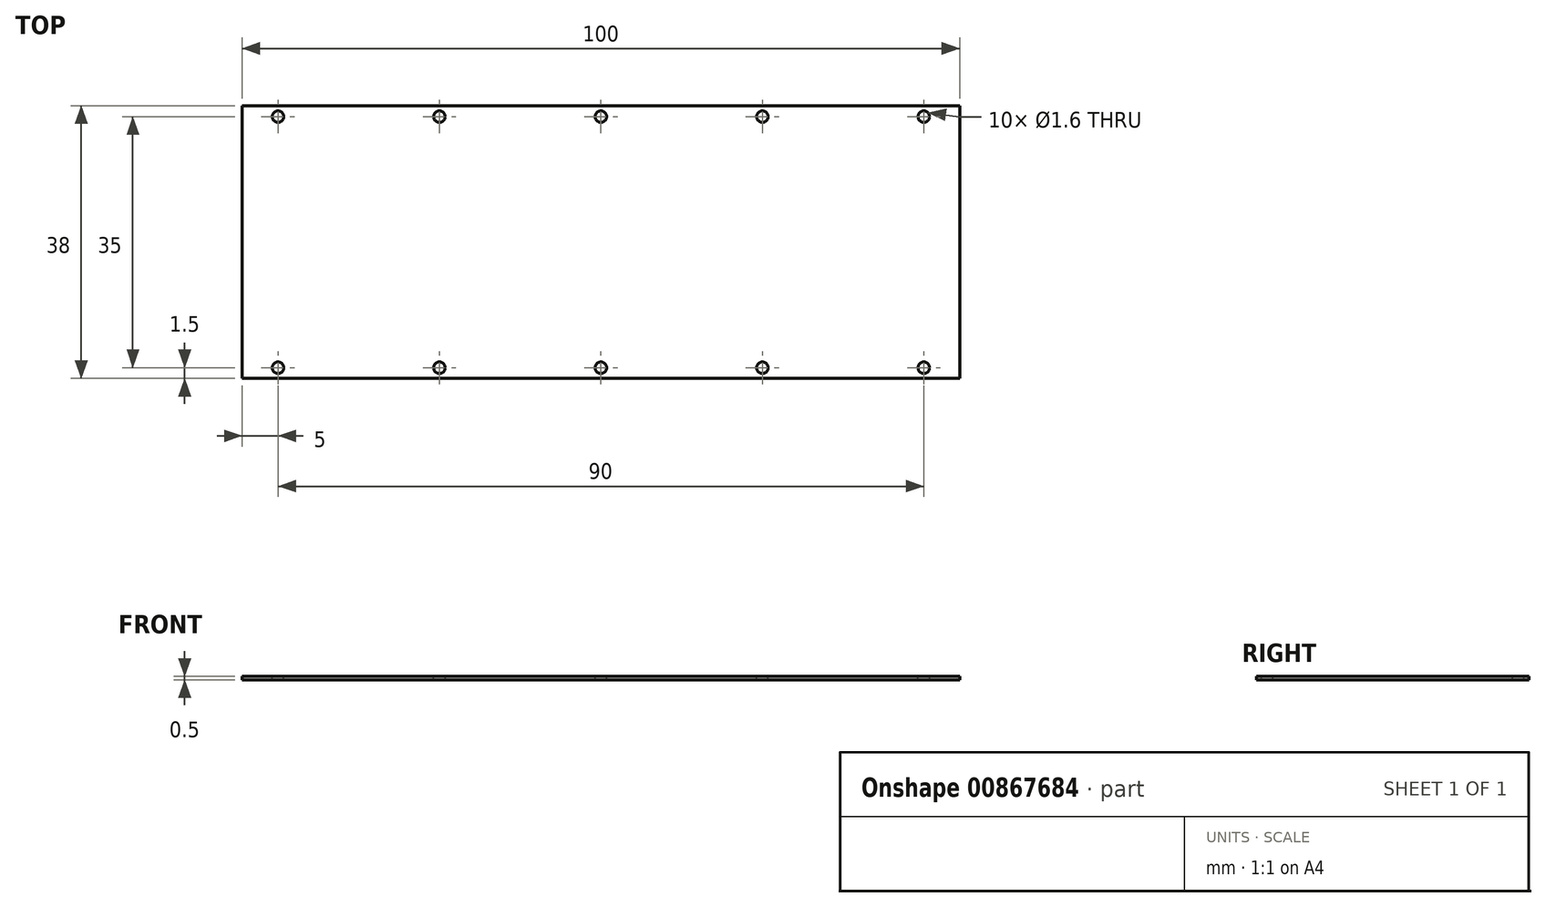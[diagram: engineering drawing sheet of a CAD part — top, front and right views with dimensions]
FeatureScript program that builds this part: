
annotation { "Feature Type Name" : "Feature", "Feature Type Description" : "" }
export const myFeature = defineFeature(function(context is Context, id is Id, definition is map)
    precondition{}
    {
        {
            var Q0;
            Q0=qCreatedBy(makeId("Top.planeOp"),FACE);
            var sketch = newSketch(context, id + "F0", { "sketchPlane" : qUnion([Q0])});
            skLineSegment(sketch, "E0.bottom", {"start": v(0, 19) * mm, "end": v(-100, 19) * mm});
            skLineSegment(sketch, "E0.top", {"start": v(0, -19) * mm, "end": v(-100, -19) * mm});
            skLineSegment(sketch, "E0.left", {"start": v(0, 19) * mm, "end": v(0, -19) * mm});
            skLineSegment(sketch, "E0.right", {"start": v(-100, 19) * mm, "end": v(-100, -19) * mm});
            skSolve(sketch);
        }
        {
            var Q0;
            Q0=makeQuery(id+"F0.imprint","IMPRINT",FACE,{"disambiguationData":[TD([[makeQuery(id+"F0.imprint","IMPRINT",EDGE,{"derivedFrom":sQuery(id+"F0.wireOp",EDGE,"E0.bottom")}),1.0]])]});
            extrude(context, id + "F1", {"entities" : qUnion([Q0]), "depth" : .5 * mm, "offsetDistance" : 25 * mm});
        }
        {
            var Q0;
            Q0=makeQuery(id+"F1.opExtrude","CAP_FACE",FACE,{"disambiguationData":[OSD([sQuery(id+"F0.wireOp",EDGE,"E0.bottom"),sQuery(id+"F0.wireOp",EDGE,"E0.top"),sQuery(id+"F0.wireOp",EDGE,"E0.left"),sQuery(id+"F0.wireOp",EDGE,"E0.right")])],"isStart":false});
            var sketch = newSketch(context, id + "F2", { "sketchPlane" : qUnion([Q0])});
            skCircle(sketch, "E1", {"center": v(-95, 17.5) * mm, "radius": 0.8 * mm});
            skCircle(sketch, "E2", {"center": v(-95, -17.5) * mm, "radius": 0.8 * mm});
            skCircle(sketch, "E3.1.0.0", {"center": v(-72.5, -17.5) * mm, "radius": 0.8 * mm});
            skCircle(sketch, "E3.2.0.0", {"center": v(-50, -17.5) * mm, "radius": 0.8 * mm});
            skCircle(sketch, "E3.3.0.0", {"center": v(-27.5, -17.5) * mm, "radius": 0.8 * mm});
            skCircle(sketch, "E3.4.0.0", {"center": v(-5, -17.5) * mm, "radius": 0.8 * mm});
            skLineSegment(sketch, "E3.direction1", {"start": v(-95, -17.5) * mm, "end": v(-72.5, -17.5) * mm, "construction": true});
            skCircle(sketch, "E4.1.0.0", {"center": v(-72.5, 17.5) * mm, "radius": 0.8 * mm});
            skCircle(sketch, "E4.2.0.0", {"center": v(-50, 17.5) * mm, "radius": 0.8 * mm});
            skCircle(sketch, "E4.3.0.0", {"center": v(-27.5, 17.5) * mm, "radius": 0.8 * mm});
            skCircle(sketch, "E4.4.0.0", {"center": v(-5, 17.5) * mm, "radius": 0.8 * mm});
            skLineSegment(sketch, "E4.direction1", {"start": v(-95, 17.5) * mm, "end": v(-72.5, 17.5) * mm, "construction": true});
            skSolve(sketch);
        }
        {
            var Q0;
            Q0=makeQuery(id+"F2.imprint","IMPRINT",FACE,{"disambiguationData":[TD([[makeQuery(id+"F2.imprint","IMPRINT",EDGE,{"derivedFrom":sQuery(id+"F2.wireOp",EDGE,"E2")}),1.0]])]});
            var Q1;
            Q1=makeQuery(id+"F2.imprint","IMPRINT",FACE,{"disambiguationData":[TD([[makeQuery(id+"F2.imprint","IMPRINT",EDGE,{"derivedFrom":sQuery(id+"F2.wireOp",EDGE,"E3.1.0.0")}),1.0]])]});
            var Q2;
            Q2=makeQuery(id+"F2.imprint","IMPRINT",FACE,{"disambiguationData":[TD([[makeQuery(id+"F2.imprint","IMPRINT",EDGE,{"derivedFrom":sQuery(id+"F2.wireOp",EDGE,"E3.2.0.0")}),1.0]])]});
            var Q3;
            Q3=makeQuery(id+"F2.imprint","IMPRINT",FACE,{"disambiguationData":[TD([[makeQuery(id+"F2.imprint","IMPRINT",EDGE,{"derivedFrom":sQuery(id+"F2.wireOp",EDGE,"E3.3.0.0")}),1.0]])]});
            var Q4;
            Q4=makeQuery(id+"F2.imprint","IMPRINT",FACE,{"disambiguationData":[TD([[makeQuery(id+"F2.imprint","IMPRINT",EDGE,{"derivedFrom":sQuery(id+"F2.wireOp",EDGE,"E3.4.0.0")}),1.0]])]});
            var Q5;
            Q5=makeQuery(id+"F2.imprint","IMPRINT",FACE,{"disambiguationData":[TD([[makeQuery(id+"F2.imprint","IMPRINT",EDGE,{"derivedFrom":sQuery(id+"F2.wireOp",EDGE,"E4.4.0.0")}),1.0]])]});
            var Q6;
            Q6=makeQuery(id+"F2.imprint","IMPRINT",FACE,{"disambiguationData":[TD([[makeQuery(id+"F2.imprint","IMPRINT",EDGE,{"derivedFrom":sQuery(id+"F2.wireOp",EDGE,"E4.3.0.0")}),1.0]])]});
            var Q7;
            Q7=makeQuery(id+"F2.imprint","IMPRINT",FACE,{"disambiguationData":[TD([[makeQuery(id+"F2.imprint","IMPRINT",EDGE,{"derivedFrom":sQuery(id+"F2.wireOp",EDGE,"E4.2.0.0")}),1.0]])]});
            var Q8;
            Q8=makeQuery(id+"F2.imprint","IMPRINT",FACE,{"disambiguationData":[TD([[makeQuery(id+"F2.imprint","IMPRINT",EDGE,{"derivedFrom":sQuery(id+"F2.wireOp",EDGE,"E4.1.0.0")}),1.0]])]});
            var Q9;
            Q9=makeQuery(id+"F2.imprint","IMPRINT",FACE,{"disambiguationData":[TD([[makeQuery(id+"F2.imprint","IMPRINT",EDGE,{"derivedFrom":sQuery(id+"F2.wireOp",EDGE,"E1")}),1.0]])]});
            extrude(context, id + "F3", {"entities" : qUnion([Q0, Q1, Q2, Q3, Q4, Q5, Q6, Q7, Q8, Q9]), "operationType" : NewBodyOperationType.REMOVE, "endBound" : BoundingType.THROUGH_ALL, "oppositeDirection" : true, "depth" : 25 * mm, "offsetDistance" : 25 * mm});
        }
    });
